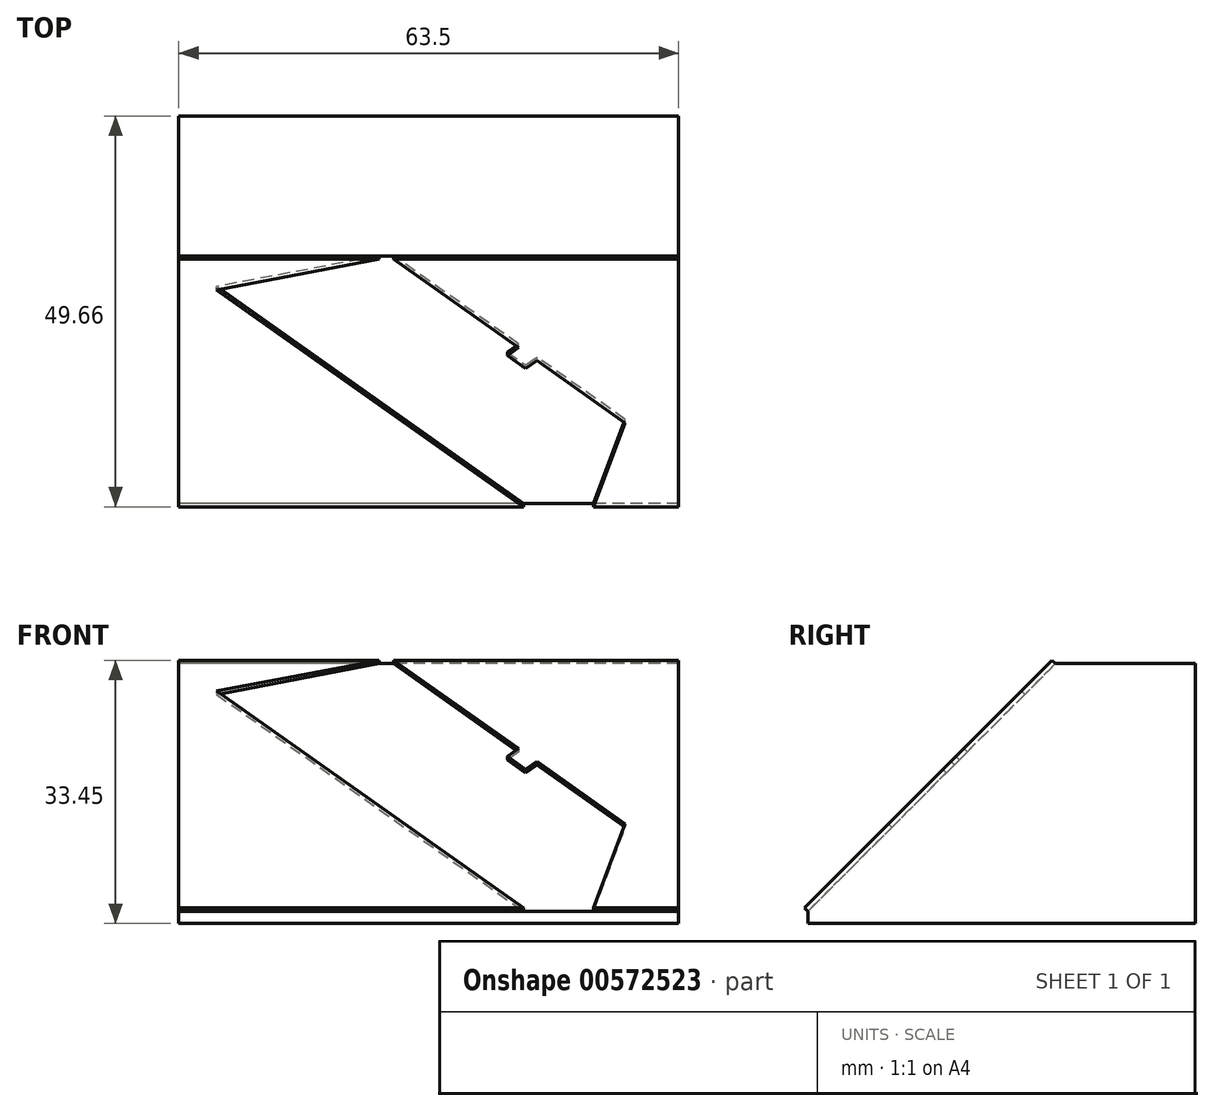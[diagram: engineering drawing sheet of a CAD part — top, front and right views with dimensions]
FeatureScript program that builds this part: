
annotation { "Feature Type Name" : "Feature", "Feature Type Description" : "" }
export const myFeature = defineFeature(function(context is Context, id is Id, definition is map)
    precondition{}
    {
        {
            var Q0;
            Q0=qCreatedBy(makeId("Right.planeOp"),FACE);
            var sketch = newSketch(context, id + "F0", { "sketchPlane" : qUnion([Q0])});
            skLineSegment(sketch, "E0", {"start": v(0, 0) * mm, "end": v(50.8, 0) * mm});
            skLineSegment(sketch, "E1", {"start": v(50.8, 0) * mm, "end": v(50.8, 50.8) * mm});
            skLineSegment(sketch, "E2", {"start": v(50.8, 50.8) * mm, "end": v(0, 0) * mm});
            skLineSegment(sketch, "E3", {"start": v(33.02, 33.02) * mm, "end": v(50.8, 33.02) * mm});
            skLineSegment(sketch, "E4", {"start": v(1.57, 0) * mm, "end": v(1.57, 1.57) * mm});
            skSolve(sketch);
        }
        {
            var Q0;
            {var subQ0=sQuery(id+"F0.wireOp",EDGE,"E3");Q0=makeQuery(id+"F0.imprint","IMPRINT",FACE,{"disambiguationData":[TD([[makeQuery(id+"F0.imprint","IMPRINT",EDGE,{"derivedFrom":subQ0}),-1.0]])]});}
            extrude(context, id + "F1", {"entities" : qUnion([Q0]), "endBound" : BoundingType.SYMMETRIC, "depth" : 63.5 * mm, "offsetDistance" : 25.4 * mm});
        }
        {
            var Q0;
            Q0=makeQuery(id+"F1.opExtrude","SWEPT_FACE",FACE,{"disambiguationData":[OSD([sQuery(id+"F0.wireOp",EDGE,"E2")])]});
            var sketch = newSketch(context, id + "F2", { "sketchPlane" : qUnion([Q0])});
            skLineSegment(sketch, "E5.0.0", {"start": v(-31.75, 46.7) * mm, "end": v(-31.75, 46.7) * mm});
            skLineSegment(sketch, "E5.0.2", {"start": v(31.75, 2.23) * mm, "end": v(31.75, 46.7) * mm});
            skLineSegment(sketch, "E5.0.3", {"start": v(31.75, 46.7) * mm, "end": v(-31.75, 46.7) * mm});
            skLineSegment(sketch, "E6", {"start": v(-26.93, 41.18) * mm, "end": v(19.05, -4.8) * mm});
            skLineSegment(sketch, "E7", {"start": v(19.05, -4.8) * mm, "end": v(24.97, 17.3) * mm});
            skLineSegment(sketch, "E8", {"start": v(24.97, 17.3) * mm, "end": v(-4.83, 47.1) * mm});
            skLineSegment(sketch, "E9", {"start": v(-4.83, 47.1) * mm, "end": v(-26.93, 41.18) * mm});
            skLineSegment(sketch, "E10.0", {"start": v(31.75, 2.23) * mm, "end": v(-31.75, 2.23) * mm});
            skLineSegment(sketch, "E11", {"start": v(10.07, 32.2) * mm, "end": v(-3.94, 18.19) * mm, "construction": true});
            skLineSegment(sketch, "E12", {"start": v(11.43, 30.84) * mm, "end": v(9.99, 29.4) * mm});
            skLineSegment(sketch, "E13", {"start": v(9.99, 29.4) * mm, "end": v(12.32, 27.07) * mm});
            skLineSegment(sketch, "E14", {"start": v(12.32, 27.07) * mm, "end": v(13.76, 28.5) * mm});
            skSolve(sketch);
        }
        {
            var Q0;
            {var subQ1=sQuery(id+"F2.wireOp",EDGE,"E5.0.2");Q0=makeQuery(id+"F2.imprint","IMPRINT",FACE,{"disambiguationData":[TD([[makeQuery(id+"F2.imprint","IMPRINT",EDGE,{"derivedFrom":subQ1}),-1.0]])]});}
            var Q1;
            {var subQ0=sQuery(id+"F2.wireOp",EDGE,"E12");Q1=makeQuery(id+"F2.imprint","IMPRINT",FACE,{"disambiguationData":[TD([[makeQuery(id+"F2.imprint","IMPRINT",EDGE,{"derivedFrom":subQ0}),1.0]])]});}
            var Q2;
            {var subQ1=makeQuery(id+"F1.opExtrude","CAP_EDGE",EDGE,{"disambiguationData":[OSD([sQuery(id+"F0.wireOp",EDGE,"E2")])],"isStart":true});Q2=makeQuery(id+"F2.imprint","IMPRINT",FACE,{"disambiguationData":[TD([[makeQuery(id+"F2.imprint","IMPRINT",EDGE,{"derivedFrom":subQ1}),1.0]])]});}
            extrude(context, id + "F3", {"entities" : qUnion([Q0, Q1, Q2]), "operationType" : NewBodyOperationType.ADD, "depth" : 0.6 * mm, "offsetDistance" : 25.4 * mm});
        }
    });
